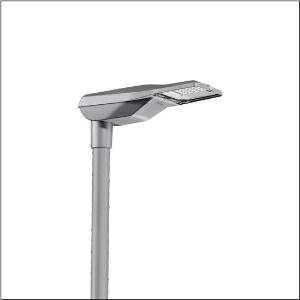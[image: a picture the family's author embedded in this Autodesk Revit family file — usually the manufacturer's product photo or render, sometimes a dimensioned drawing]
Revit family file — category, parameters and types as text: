
# Revit family: streetlight_sl_21_iq_micro___p0_8a_5xe1u31d08db_7b75
name_source: partatom
category: Lighting Fixtures
units: mm (PartAtom-declared; Revit-internal decimal feet)

## family parameters
Cut with Voids When Loaded = No
Host = Face
Light Source = No
Part Type = Normal
Room Calculation Point = No
Round Connector Dimension = Use Diameter
Shared = No

## types (1)
- --- (1 x LED, 4750 lm, 36.4 W, 3000K)
    Apparent Load = 36 VA
    CIE Flux Codes = 33 69 96 100 100
    Color Rendering = 70
    Color Temperature = 3000K
    Default Elevation = 1800 mm
    Description = Streetlight SL 21 iQ micro, mast luminaire, primary light control with lens, of PMMA, primary optical cover: cover, of toughened safety glass, transparent, light distribution: P0.8a, light emission: direct distribution, primary light characteristic: asymmetric, installation type: post-top, side-entry, LED, High Power LED, rated luminous flux: 4.750lm, luminous efficacy: 131lm/W, light colour: 730, colour temperature: 3000K, control gear: iQ-Comfort, control: pre-setting: linear dimming characteristic, Auto-Match, Temp-Guard, Lumen-Switch, Night-Set, Smart-Wire, Light-Fading, Desk-Remote (wireless, voltage-free reading and setting of iQ features in the workshop via application-optimized NFC function/RFID function), optimised constant luminous flux control (CLO 2.0), mains connection: 220..240V, AC, 50/60Hz, start of lifetime: 36W, end of service life: 38W, reduction: 16W, luminaire housing, of diecast aluminium, powder-coated, Siteco® metallic grey (DB 702S), corrosivity category C5 high according to DIN EN ISO 12944, please order mast flange separately, inclination adjustable: 0°, 5°, 10°, 15°, sealing non-destructively replaceable, multi-level sealing system, length: 528mm, width: 235mm, height: 110mm, mast flange for spigot size: 42mm (side-entry): 5XC10008XM4, 60/48mm (side-entry/post-top): 5XC10108XM2, 76/60mm (side-entry/post-top): 5XC10108XM1, protection rating (complete): IP66, insulation class (complete): insulation class II (safety insulation), certification: CE, ENEC, ENEC+, VDE, impact resistance: IK10, permissible operating ambient temperature for outdoor applications: -40..+50°C, standard-compliant lighting for roads and squares, packaging unit: 1 piece

Light Distribution: P0.8a
    Height = 110 mm
    Lamp = 1 x LED
    Lamp Light Flux = 4750 lm
    Lamp Power = 36.4 W
    Lamp count = 1
    Length = 528 mm
    Luminous efficacy = 130 lm/W
    Manufacturer = Siteco
    ModVariant = No
    Model = 5XE1U31D08DB
    Number of Poles = 1
    OnlyDefault = Yes
    Power Factor = 1
    Product Name = Streetlight SL 21 iQ micro | P0.8a
    Product group = mast luminaire | pylon top
    ProductGroupID = 6100
    Protection Class = Protection class II
    Protection Degree = IP 66
    RLX_Detail_Level = 1
    RLX_Emergency_Light_Flux = 0 lm
    RLX_Emergency_Type = 0
    RLX_Emergency_Type_DB = No
    RlxData = <blob elided: 99617 chars, md5=fe0ccbb7>
    Socket = socket
    Standby Power = 0 W
    System Light Flux = 4750 lm
    System Power = 36 W
    Type Comments = factory setting: luminous flux: 100 % | dim-lin: 254 | 715 mA
    Type Image = l_1006881.jpg
    URL = http://relux.com
    VarID = @adj_083533
    Voltage = 0 V
    Weight = 0.00 kg
    Width = 235 mm

## geometry (parser evidence)
native form markers: Blend x4, Sweep x11
no freeform markers — native parametric forms only
